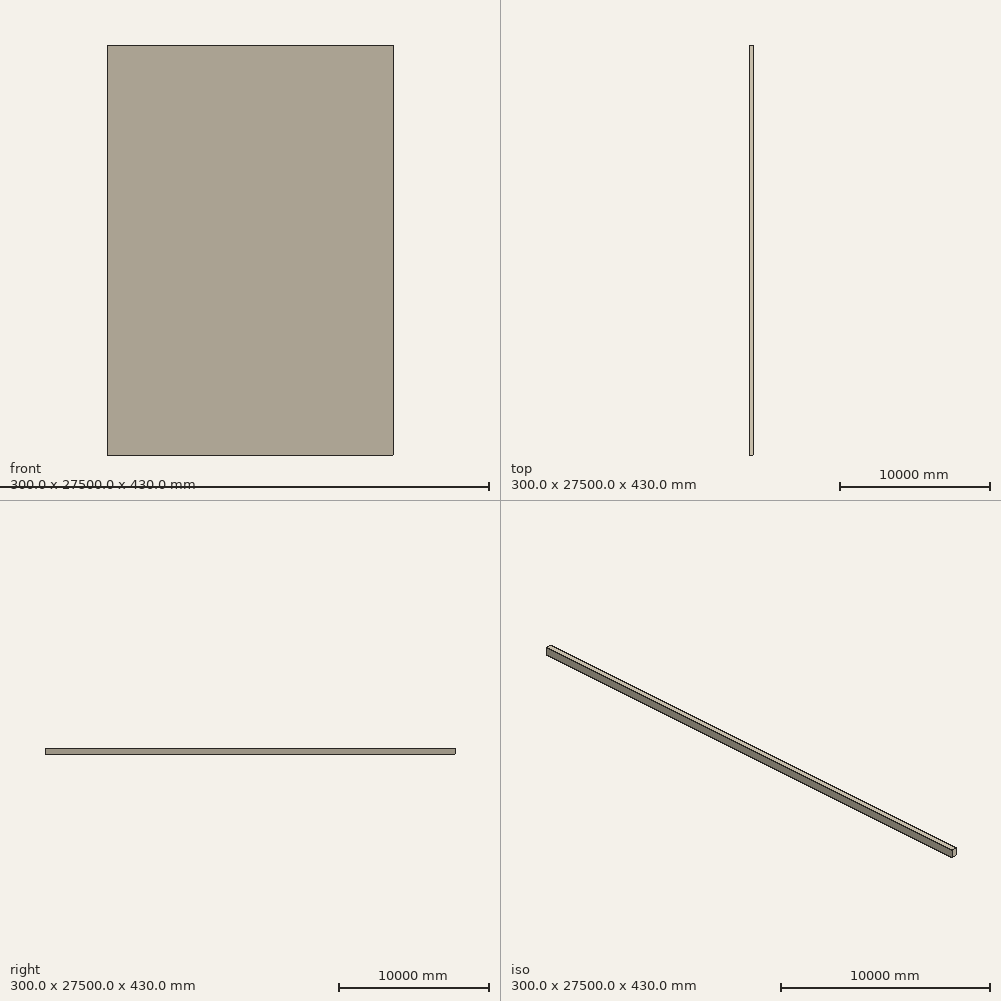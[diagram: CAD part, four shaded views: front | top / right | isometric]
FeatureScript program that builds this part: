
annotation { "Feature Type Name" : "Feature", "Feature Type Description" : "" }
export const myFeature = defineFeature(function(context is Context, id is Id, definition is map)
    precondition{}
    {
        {
            var Q0;
            Q0=qCreatedBy(makeId("Front.planeOp"),FACE);
            var sketch = newSketch(context, id + "F0", { "sketchPlane" : qUnion([Q0])});
            skLineSegment(sketch, "E0.bottom", {"start": v(-300, -215) * mm, "end": v(300, -215) * mm});
            skLineSegment(sketch, "E0.top", {"start": v(-300, 215) * mm, "end": v(300, 215) * mm});
            skLineSegment(sketch, "E0.left", {"start": v(-300, -215) * mm, "end": v(-300, 215) * mm});
            skLineSegment(sketch, "E0.right", {"start": v(300, -215) * mm, "end": v(300, 215) * mm});
            skPoint(sketch, "E0.middle", {"position": v(0, 0) * mm});
            skLineSegment(sketch, "E1", {"start": v(0, 0) * mm, "end": v(0, 215) * mm});
            skLineSegment(sketch, "E2", {"start": v(0, 215) * mm, "end": v(0, -215) * mm});
            skSolve(sketch);
        }
        {
            var Q0;
            {var subQ4=sQuery(id+"F0.wireOp",EDGE,"E0.left");Q0=makeQuery(id+"F0.imprint","IMPRINT",FACE,{"disambiguationData":[TD([[makeQuery(id+"F0.imprint","IMPRINT",EDGE,{"derivedFrom":subQ4}),-1.0]])]});}
            extrude(context, id + "F1", {"entities" : qUnion([Q0]), "depth" : 27500 * mm});
        }
    });
